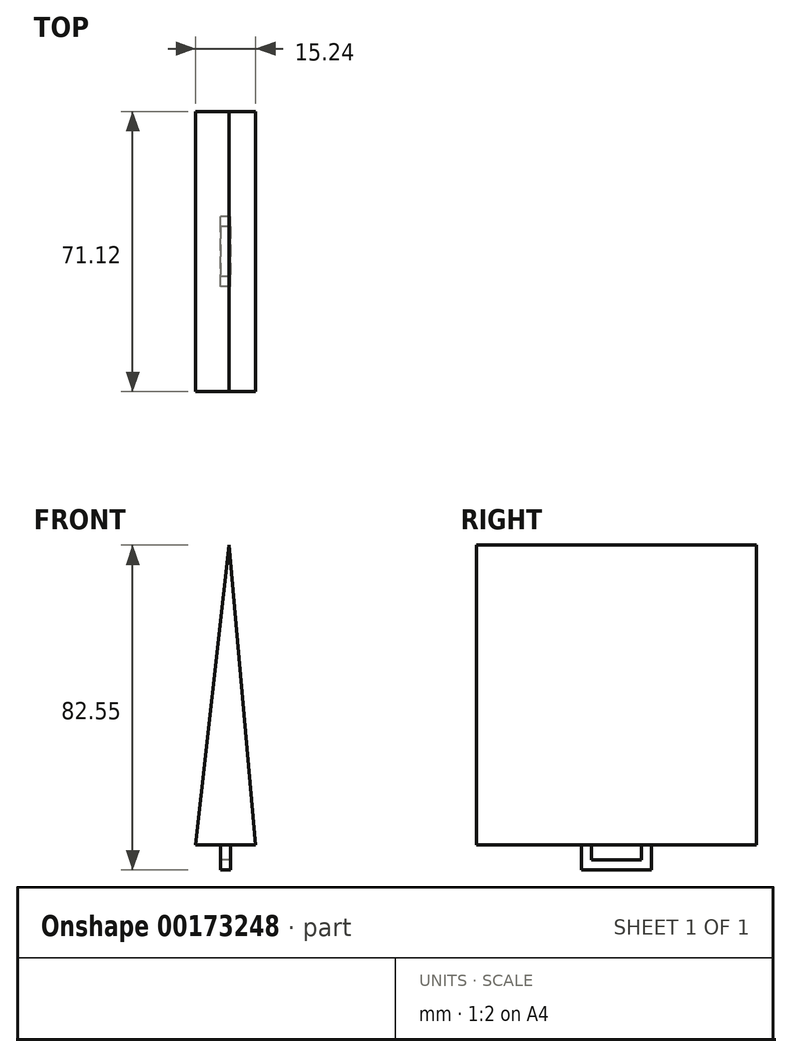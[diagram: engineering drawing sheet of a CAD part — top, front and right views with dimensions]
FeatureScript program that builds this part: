
annotation { "Feature Type Name" : "Feature", "Feature Type Description" : "" }
export const myFeature = defineFeature(function(context is Context, id is Id, definition is map)
    precondition{}
    {
        {
            var Q0;
            Q0=qCreatedBy(makeId("Front.planeOp"),FACE);
            var sketch = newSketch(context, id + "F0", { "sketchPlane" : qUnion([Q0])});
            skLineSegment(sketch, "E0", {"start": v(0, 0) * mm, "end": v(8.51, 76.2) * mm});
            skLineSegment(sketch, "E1", {"start": v(8.51, 76.2) * mm, "end": v(15.24, 0) * mm});
            skLineSegment(sketch, "E2", {"start": v(15.24, 0) * mm, "end": v(0, 0) * mm});
            skSolve(sketch);
        }
        {
            var Q0;
            Q0=makeQuery(id+"F0.imprint","IMPRINT",FACE,{"disambiguationData":[TD([[makeQuery(id+"F0.imprint","IMPRINT",EDGE,{"derivedFrom":sQuery(id+"F0.wireOp",EDGE,"E0")}),-1.0]])]});
            extrude(context, id + "F1", {"entities" : qUnion([Q0]), "depth" : 71.12 * mm});
        }
        {
            var Q0;
            Q0=makeQuery(id+"F1.opExtrude","SWEPT_FACE",FACE,{"disambiguationData":[OSD([sQuery(id+"F0.wireOp",EDGE,"E2")])]});
            var sketch = newSketch(context, id + "F2", { "sketchPlane" : qUnion([Q0])});
            skLineSegment(sketch, "E3", {"start": v(7.62, 71.12) * mm, "end": v(7.62, 0) * mm});
            skLineSegment(sketch, "E4", {"start": v(0, 35.56) * mm, "end": v(15.24, 35.56) * mm});
            skLineSegment(sketch, "E5", {"start": v(0, 43.18) * mm, "end": v(15.24, 43.18) * mm});
            skLineSegment(sketch, "E6", {"start": v(0, 27.94) * mm, "end": v(15.24, 27.94) * mm});
            skLineSegment(sketch, "E7.bottom", {"start": v(8.89, 44.45) * mm, "end": v(6.35, 44.45) * mm});
            skLineSegment(sketch, "E7.top", {"start": v(8.89, 41.91) * mm, "end": v(6.35, 41.91) * mm});
            skLineSegment(sketch, "E7.left", {"start": v(8.89, 44.45) * mm, "end": v(8.89, 41.91) * mm});
            skLineSegment(sketch, "E7.right", {"start": v(6.35, 44.45) * mm, "end": v(6.35, 41.91) * mm});
            skPoint(sketch, "E7.middle", {"position": v(7.62, 43.18) * mm});
            skLineSegment(sketch, "E8.bottom", {"start": v(8.89, 29.21) * mm, "end": v(6.35, 29.21) * mm});
            skLineSegment(sketch, "E8.top", {"start": v(8.89, 26.67) * mm, "end": v(6.35, 26.67) * mm});
            skLineSegment(sketch, "E8.left", {"start": v(8.89, 29.21) * mm, "end": v(8.89, 26.67) * mm});
            skLineSegment(sketch, "E8.right", {"start": v(6.35, 29.21) * mm, "end": v(6.35, 26.67) * mm});
            skPoint(sketch, "E8.middle", {"position": v(7.62, 27.94) * mm});
            skSolve(sketch);
        }
        {
            var Q0;
            {var subQ0=sQuery(id+"F2.wireOp",EDGE,"E5");var subQ1=sQuery(id+"F2.wireOp",EDGE,"E3");var subQ2=makeQuery(id+"F2.imprint","INTERSECT",VERTEX,{"derivedFrom":[subQ1,subQ0]});Q0=makeQuery(id+"F2.imprint","IMPRINT",FACE,{"disambiguationData":[TD([[makeQuery(id+"F2.imprint","IMPRINT",EDGE,{"disambiguationData":[TD([[subQ2,-1.0]])],"derivedFrom":subQ1}),1.0]])]});}
            var Q1;
            {var subQ0=sQuery(id+"F2.wireOp",EDGE,"E7.bottom");var subQ1=sQuery(id+"F2.wireOp",EDGE,"E3");var subQ2=makeQuery(id+"F2.imprint","INTERSECT",VERTEX,{"derivedFrom":[subQ1,subQ0]});Q1=makeQuery(id+"F2.imprint","IMPRINT",FACE,{"disambiguationData":[TD([[makeQuery(id+"F2.imprint","IMPRINT",EDGE,{"disambiguationData":[TD([[subQ2,-1.0]])],"derivedFrom":subQ1}),1.0]])]});}
            var Q2;
            {var subQ0=sQuery(id+"F2.wireOp",EDGE,"E7.bottom");var subQ1=sQuery(id+"F2.wireOp",EDGE,"E3");var subQ2=makeQuery(id+"F2.imprint","INTERSECT",VERTEX,{"derivedFrom":[subQ1,subQ0]});Q2=makeQuery(id+"F2.imprint","IMPRINT",FACE,{"disambiguationData":[TD([[makeQuery(id+"F2.imprint","IMPRINT",EDGE,{"disambiguationData":[TD([[subQ2,-1.0]])],"derivedFrom":subQ1}),-1.0]])]});}
            var Q3;
            {var subQ0=sQuery(id+"F2.wireOp",EDGE,"E5");var subQ1=sQuery(id+"F2.wireOp",EDGE,"E3");var subQ2=makeQuery(id+"F2.imprint","INTERSECT",VERTEX,{"derivedFrom":[subQ1,subQ0]});Q3=makeQuery(id+"F2.imprint","IMPRINT",FACE,{"disambiguationData":[TD([[makeQuery(id+"F2.imprint","IMPRINT",EDGE,{"disambiguationData":[TD([[subQ2,-1.0]])],"derivedFrom":subQ1}),-1.0]])]});}
            var Q4;
            {var subQ0=sQuery(id+"F2.wireOp",EDGE,"E8.bottom");var subQ1=sQuery(id+"F2.wireOp",EDGE,"E3");var subQ2=makeQuery(id+"F2.imprint","INTERSECT",VERTEX,{"derivedFrom":[subQ1,subQ0]});Q4=makeQuery(id+"F2.imprint","IMPRINT",FACE,{"disambiguationData":[TD([[makeQuery(id+"F2.imprint","IMPRINT",EDGE,{"disambiguationData":[TD([[subQ2,-1.0]])],"derivedFrom":subQ1}),1.0]])]});}
            var Q5;
            {var subQ0=sQuery(id+"F2.wireOp",EDGE,"E8.bottom");var subQ1=sQuery(id+"F2.wireOp",EDGE,"E3");var subQ2=makeQuery(id+"F2.imprint","INTERSECT",VERTEX,{"derivedFrom":[subQ1,subQ0]});Q5=makeQuery(id+"F2.imprint","IMPRINT",FACE,{"disambiguationData":[TD([[makeQuery(id+"F2.imprint","IMPRINT",EDGE,{"disambiguationData":[TD([[subQ2,-1.0]])],"derivedFrom":subQ1}),-1.0]])]});}
            var Q6;
            {var subQ0=sQuery(id+"F2.wireOp",EDGE,"E6");var subQ1=sQuery(id+"F2.wireOp",EDGE,"E3");var subQ2=makeQuery(id+"F2.imprint","INTERSECT",VERTEX,{"derivedFrom":[subQ1,subQ0]});Q6=makeQuery(id+"F2.imprint","IMPRINT",FACE,{"disambiguationData":[TD([[makeQuery(id+"F2.imprint","IMPRINT",EDGE,{"disambiguationData":[TD([[subQ2,-1.0]])],"derivedFrom":subQ1}),-1.0]])]});}
            var Q7;
            {var subQ0=sQuery(id+"F2.wireOp",EDGE,"E6");var subQ1=sQuery(id+"F2.wireOp",EDGE,"E3");var subQ2=makeQuery(id+"F2.imprint","INTERSECT",VERTEX,{"derivedFrom":[subQ1,subQ0]});Q7=makeQuery(id+"F2.imprint","IMPRINT",FACE,{"disambiguationData":[TD([[makeQuery(id+"F2.imprint","IMPRINT",EDGE,{"disambiguationData":[TD([[subQ2,-1.0]])],"derivedFrom":subQ1}),1.0]])]});}
            extrude(context, id + "F3", {"entities" : qUnion([Q0, Q1, Q2, Q3, Q4, Q5, Q6, Q7]), "operationType" : NewBodyOperationType.ADD, "depth" : 6.35 * mm});
        }
        {
            var Q0;
            Q0=makeQuery(id+"F3.opExtrude","SWEPT_FACE",FACE,{"disambiguationData":[OSD([sQuery(id+"F2.wireOp",EDGE,"E7.bottom")])]});
            var sketch = newSketch(context, id + "F4", { "sketchPlane" : qUnion([Q0])});
            skLineSegment(sketch, "E9.bottom", {"start": v(6.35, -6.35) * mm, "end": v(8.89, -6.35) * mm});
            skLineSegment(sketch, "E9.top", {"start": v(6.35, -3.81) * mm, "end": v(8.89, -3.81) * mm});
            skLineSegment(sketch, "E9.left", {"start": v(6.35, -6.35) * mm, "end": v(6.35, -3.81) * mm});
            skLineSegment(sketch, "E9.right", {"start": v(8.89, -6.35) * mm, "end": v(8.89, -3.81) * mm});
            skSolve(sketch);
        }
        {
            var Q0;
            Q0=makeQuery(id+"F4.imprint","IMPRINT",FACE,{"disambiguationData":[TD([[makeQuery(id+"F4.imprint","IMPRINT",EDGE,{"derivedFrom":sQuery(id+"F4.wireOp",EDGE,"E9.bottom")}),-1.0]])]});
            extrude(context, id + "F5", {"entities" : qUnion([Q0]), "operationType" : NewBodyOperationType.ADD, "oppositeDirection" : true, "depth" : 17.78 * mm});
        }
    });
